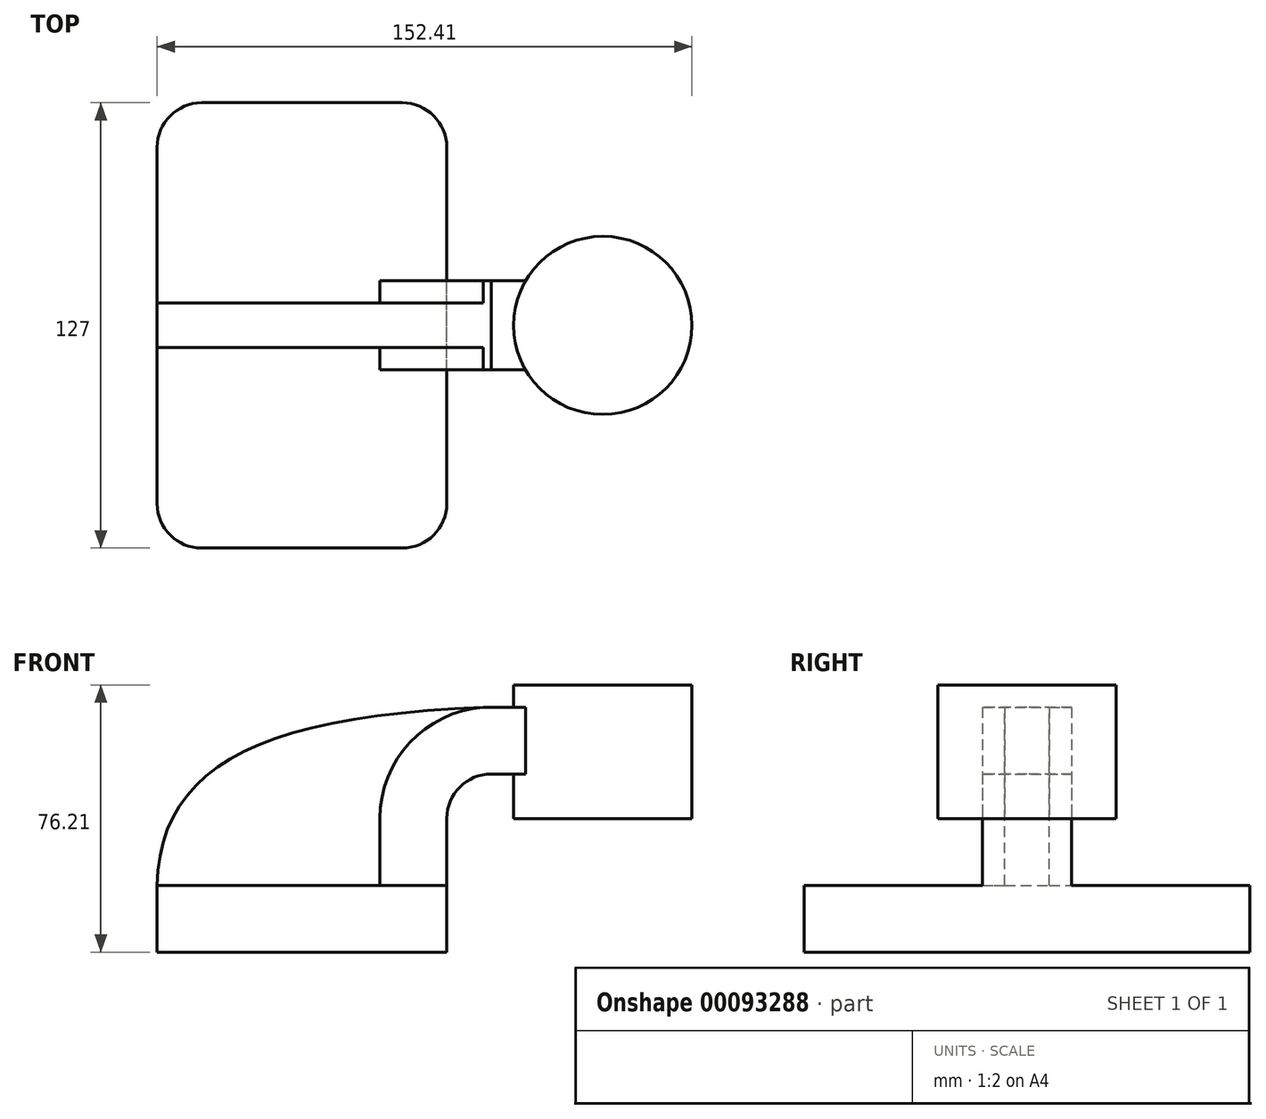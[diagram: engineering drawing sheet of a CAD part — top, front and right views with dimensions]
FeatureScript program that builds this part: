
annotation { "Feature Type Name" : "Feature", "Feature Type Description" : "" }
export const myFeature = defineFeature(function(context is Context, id is Id, definition is map)
    precondition{}
    {
        {
            var Q0;
            Q0=qCreatedBy(makeId("Front.planeOp"),FACE);
            var sketch = newSketch(context, id + "F0", { "sketchPlane" : qUnion([Q0])});
            skLineSegment(sketch, "E0.bottom", {"start": v(41.27, 9.53) * mm, "end": v(-41.27, 9.53) * mm});
            skLineSegment(sketch, "E0.top", {"start": v(41.28, -9.52) * mm, "end": v(-41.27, -9.53) * mm});
            skLineSegment(sketch, "E0.left", {"start": v(41.28, 9.53) * mm, "end": v(41.28, -9.52) * mm});
            skLineSegment(sketch, "E0.right", {"start": v(-41.28, 9.53) * mm, "end": v(-41.27, -9.53) * mm});
            skPoint(sketch, "E0.middle", {"position": v(0, 0) * mm});
            skLineSegment(sketch, "E1.bottom", {"start": v(60.32, 66.68) * mm, "end": v(111.12, 66.68) * mm});
            skLineSegment(sketch, "E1.top", {"start": v(60.33, 28.58) * mm, "end": v(111.12, 28.58) * mm});
            skLineSegment(sketch, "E1.left", {"start": v(60.33, 66.68) * mm, "end": v(60.33, 28.58) * mm});
            skLineSegment(sketch, "E1.right", {"start": v(111.12, 66.68) * mm, "end": v(111.12, 28.58) * mm});
            skPoint(sketch, "E1.middle", {"position": v(85.72, 47.63) * mm});
            skLineSegment(sketch, "E2", {"start": v(41.27, 9.53) * mm, "end": v(41.27, 28.58) * mm});
            skArc(sketch, "E3", {"start": v(41.27, 28.58) * mm, "mid": v(45, 37.56) * mm, "end": v(53.97, 41.28) * mm});
            skLineSegment(sketch, "E4", {"start": v(53.97, 41.28) * mm, "end": v(85.72, 41.28) * mm});
            skLineSegment(sketch, "E5.0", {"start": v(53.97, 60.33) * mm, "end": v(85.72, 60.33) * mm});
            skArc(sketch, "E5.1", {"start": v(22.22, 28.58) * mm, "mid": v(31.52, 51.03) * mm, "end": v(53.97, 60.33) * mm});
            skLineSegment(sketch, "E5.2", {"start": v(22.22, 9.53) * mm, "end": v(22.22, 28.58) * mm});
            skLineSegment(sketch, "E6", {"start": v(85.73, 28.58) * mm, "end": v(85.72, 66.68) * mm});
            skFitSpline(sketch, "E7", {"points": [v(-41.28, 9.52) * mm, v(53.97, 60.33) * mm], "startDerivative": vector(2.66, 102.31) * mm, "endDerivative": vector(197.82, 6.6) * mm});
            skSolve(sketch);
        }
        {
            var Q0;
            Q0=makeQuery(id+"F0.imprint","IMPRINT",FACE,{"disambiguationData":[TD([[makeQuery(id+"F0.imprint","IMPRINT",EDGE,{"derivedFrom":sQuery(id+"F0.wireOp",EDGE,"E0.top")}),-1.0]])]});
            extrude(context, id + "F1", {"entities" : qUnion([Q0]), "endBound" : BoundingType.SYMMETRIC, "depth" : 127 * mm});
        }
        {
            var Q0;
            {var subQ1=sQuery(id+"F0.wireOp",EDGE,"E2");Q0=makeQuery(id+"F0.imprint","IMPRINT",FACE,{"disambiguationData":[TD([[makeQuery(id+"F0.imprint","IMPRINT",EDGE,{"derivedFrom":subQ1}),1.0]])]});}
            var Q1;
            {var subQ0=sQuery(id+"F0.wireOp",EDGE,"E5.0");var subQ1=sQuery(id+"F0.wireOp",EDGE,"E1.left");var subQ2=makeQuery(id+"F0.imprint","INTERSECT",VERTEX,{"derivedFrom":[subQ1,subQ0]});Q1=makeQuery(id+"F0.imprint","IMPRINT",FACE,{"disambiguationData":[TD([[makeQuery(id+"F0.imprint","IMPRINT",EDGE,{"disambiguationData":[TD([[subQ2,-1.0]])],"derivedFrom":subQ1}),1.0]])]});}
            extrude(context, id + "F2", {"entities" : qUnion([Q0, Q1]), "operationType" : NewBodyOperationType.ADD, "endBound" : BoundingType.SYMMETRIC, "depth" : 25.4 * mm});
        }
        {
            var Q0;
            {var subQ3=sQuery(id+"F0.wireOp",EDGE,"E5.2");Q0=makeQuery(id+"F0.imprint","IMPRINT",FACE,{"disambiguationData":[TD([[makeQuery(id+"F0.imprint","IMPRINT",EDGE,{"derivedFrom":subQ3}),1.0]])]});}
            extrude(context, id + "F3", {"entities" : qUnion([Q0]), "operationType" : NewBodyOperationType.ADD, "endBound" : BoundingType.SYMMETRIC, "depth" : 12.7 * mm});
        }
        {
            var Q0;
            {var subQ0=sQuery(id+"F0.wireOp",EDGE,"E1.right");Q0=makeQuery(id+"F0.imprint","IMPRINT",FACE,{"disambiguationData":[TD([[makeQuery(id+"F0.imprint","IMPRINT",EDGE,{"derivedFrom":subQ0}),-1.0]])]});}
            var Q1;
            Q1=sQuery(id+"F0.wireOp",EDGE,"E6");
            revolve(context, id + "F4", {"operationType" : NewBodyOperationType.ADD, "entities" : qUnion([Q0]), "axis" : qUnion([Q1]), "revolveType" : RevolveType.FULL});
        }
        {
            var Q0;
            Q0=makeQuery(id+"F1.opExtrude","CAP_EDGE",EDGE,{"disambiguationData":[OSD([sQuery(id+"F0.wireOp",EDGE,"E0.right")])],"isStart":false});
            var Q1;
            Q1=makeQuery(id+"F1.opExtrude","CAP_EDGE",EDGE,{"disambiguationData":[OSD([sQuery(id+"F0.wireOp",EDGE,"E0.left")])],"isStart":false});
            var Q2;
            Q2=makeQuery(id+"F1.opExtrude","CAP_EDGE",EDGE,{"disambiguationData":[OSD([sQuery(id+"F0.wireOp",EDGE,"E0.left")])],"isStart":true});
            var Q3;
            Q3=makeQuery(id+"F1.opExtrude","CAP_EDGE",EDGE,{"disambiguationData":[OSD([sQuery(id+"F0.wireOp",EDGE,"E0.right")])],"isStart":true});
            fillet(context, id + "F5", {"entities" : qUnion([Q0, Q1, Q2, Q3]), "radius" : 12.7 * mm, "tangentPropagation" : true, "allowEdgeOverflow" : false});
        }
    });
